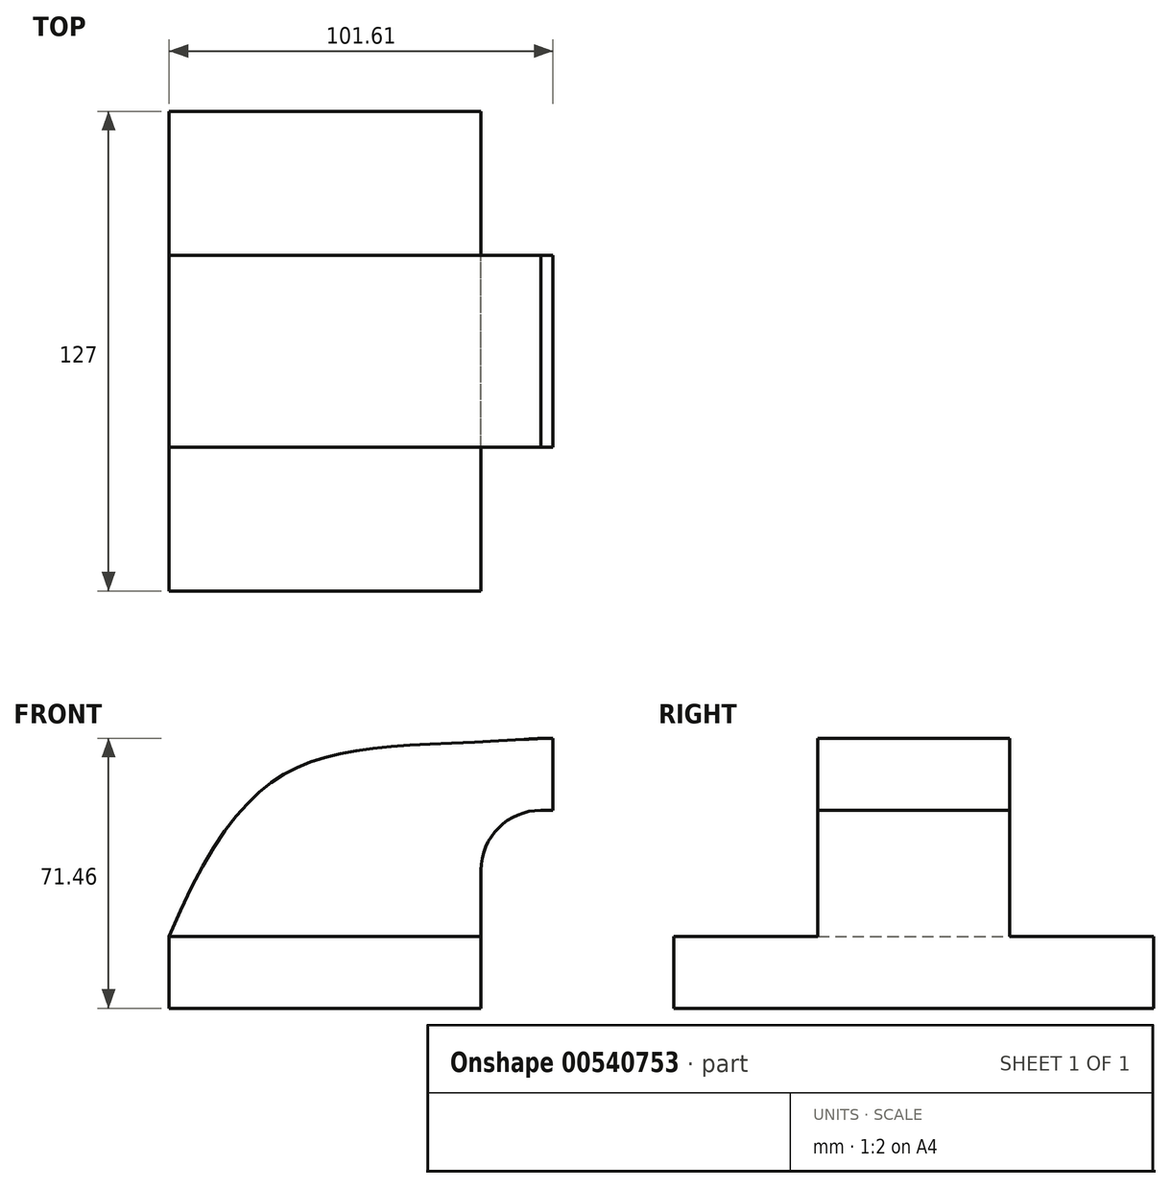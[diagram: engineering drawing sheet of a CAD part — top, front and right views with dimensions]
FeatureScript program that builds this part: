
annotation { "Feature Type Name" : "Feature", "Feature Type Description" : "" }
export const myFeature = defineFeature(function(context is Context, id is Id, definition is map)
    precondition{}
    {
        {
            var Q0;
            Q0=qCreatedBy(makeId("Front.planeOp"),FACE);
            var sketch = newSketch(context, id + "F0", { "sketchPlane" : qUnion([Q0])});
            skLineSegment(sketch, "E0.bottom", {"start": v(-41.28, 9.52) * mm, "end": v(41.27, 9.53) * mm});
            skLineSegment(sketch, "E0.top", {"start": v(-41.28, -9.53) * mm, "end": v(41.28, -9.53) * mm});
            skLineSegment(sketch, "E0.left", {"start": v(-41.28, 9.52) * mm, "end": v(-41.27, -9.53) * mm});
            skLineSegment(sketch, "E0.right", {"start": v(41.28, 9.53) * mm, "end": v(41.28, -9.52) * mm});
            skPoint(sketch, "E0.middle", {"position": v(0, 0) * mm});
            skLineSegment(sketch, "E1.bottom", {"start": v(60.32, 38.1) * mm, "end": v(111.12, 38.1) * mm});
            skLineSegment(sketch, "E1.top", {"start": v(60.33, 66.67) * mm, "end": v(111.12, 66.67) * mm});
            skLineSegment(sketch, "E1.left", {"start": v(60.32, 38.1) * mm, "end": v(60.32, 66.67) * mm});
            skLineSegment(sketch, "E1.right", {"start": v(111.12, 38.1) * mm, "end": v(111.12, 66.68) * mm});
            skPoint(sketch, "E1.middle", {"position": v(85.72, 52.39) * mm});
            skLineSegment(sketch, "E2", {"start": v(41.27, 9.53) * mm, "end": v(41.27, 27) * mm});
            skArc(sketch, "E3", {"start": v(41.27, 27) * mm, "mid": v(45.92, 38.23) * mm, "end": v(57.15, 42.88) * mm});
            skLineSegment(sketch, "E4", {"start": v(57.15, 42.88) * mm, "end": v(85.72, 42.88) * mm});
            skLineSegment(sketch, "E5.0", {"start": v(57.15, 61.93) * mm, "end": v(85.72, 61.93) * mm});
            skArc(sketch, "E5.1", {"start": v(22.23, 27) * mm, "mid": v(32.45, 51.7) * mm, "end": v(57.15, 61.93) * mm});
            skLineSegment(sketch, "E5.2", {"start": v(22.22, 9.53) * mm, "end": v(22.22, 27) * mm});
            skFitSpline(sketch, "E6", {"points": [v(-41.28, 9.52) * mm, v(57.15, 61.93) * mm], "startDerivative": vector(71.82, 169.03) * mm, "endDerivative": vector(171.45, 11.57) * mm});
            skSolve(sketch);
        }
        {
            var Q0;
            Q0=makeQuery(id+"F0.imprint","IMPRINT",FACE,{"disambiguationData":[TD([[makeQuery(id+"F0.imprint","IMPRINT",EDGE,{"derivedFrom":sQuery(id+"F0.wireOp",EDGE,"E0.top")}),1.0]])]});
            extrude(context, id + "F1", {"entities" : qUnion([Q0]), "endBound" : BoundingType.SYMMETRIC, "depth" : 127 * mm, "offsetDistance" : 25.4 * mm});
        }
        {
            var Q0;
            {var subQ3=sQuery(id+"F0.wireOp",EDGE,"E5.2");Q0=makeQuery(id+"F0.imprint","IMPRINT",FACE,{"disambiguationData":[TD([[makeQuery(id+"F0.imprint","IMPRINT",EDGE,{"derivedFrom":subQ3}),1.0]])]});}
            var Q1;
            {var subQ1=sQuery(id+"F0.wireOp",EDGE,"E2");Q1=makeQuery(id+"F0.imprint","IMPRINT",FACE,{"disambiguationData":[TD([[makeQuery(id+"F0.imprint","IMPRINT",EDGE,{"derivedFrom":subQ1}),1.0]])]});}
            extrude(context, id + "F2", {"entities" : qUnion([Q0, Q1]), "operationType" : NewBodyOperationType.ADD, "endBound" : BoundingType.SYMMETRIC, "depth" : 50.8 * mm, "offsetDistance" : 25.4 * mm});
        }
    });
